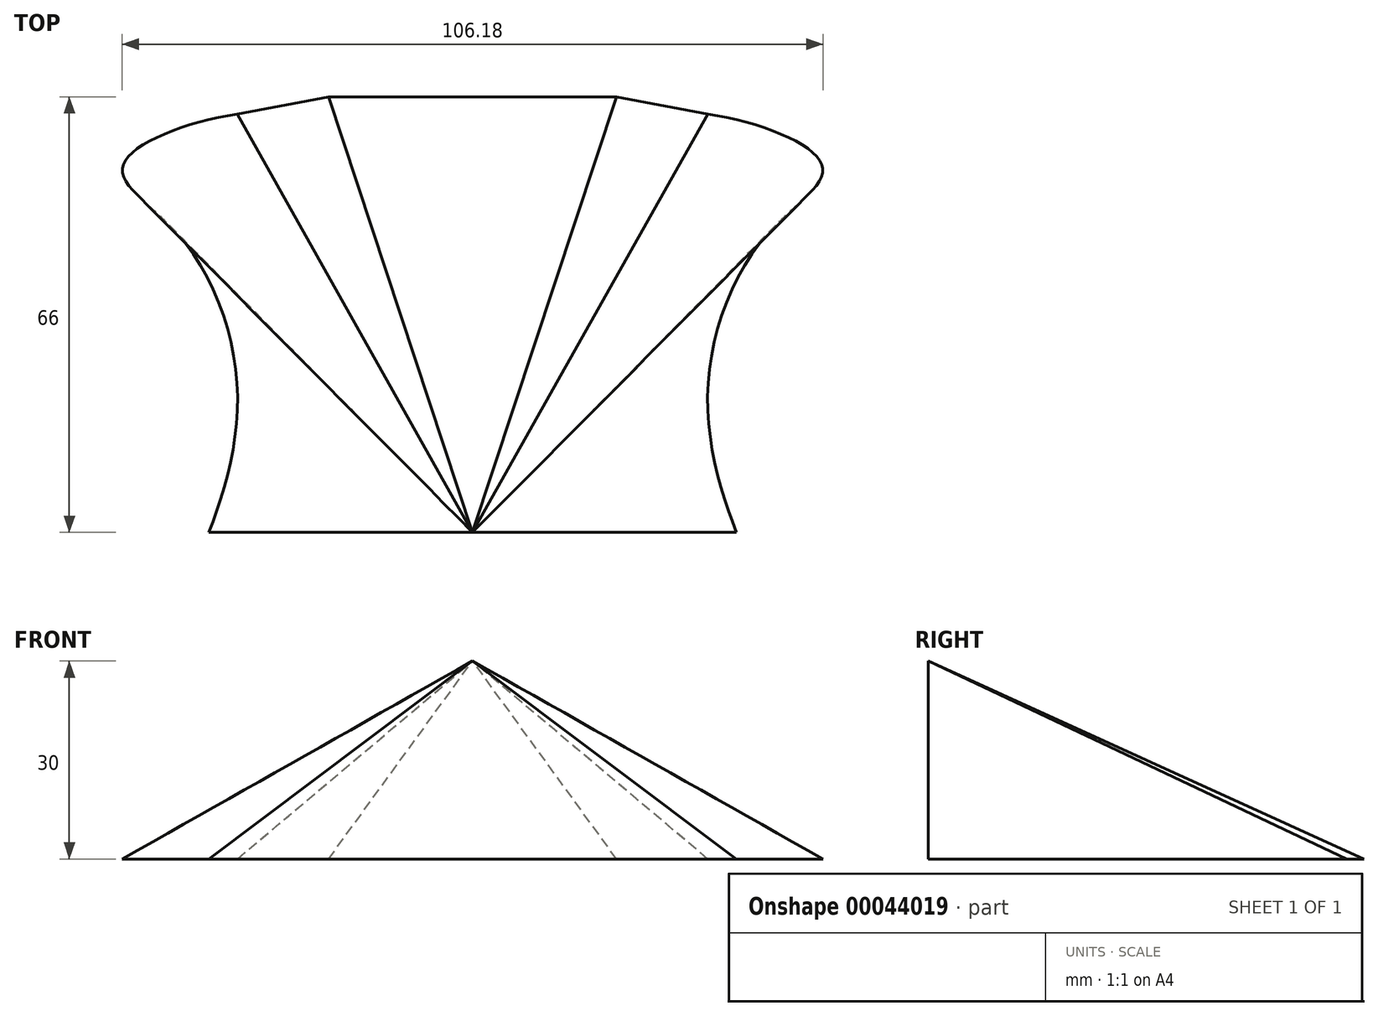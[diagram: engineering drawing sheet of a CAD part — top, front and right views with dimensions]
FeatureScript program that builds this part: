
annotation { "Feature Type Name" : "Feature", "Feature Type Description" : "" }
export const myFeature = defineFeature(function(context is Context, id is Id, definition is map)
    precondition{}
    {
        {
            var Q0;
            Q0=qCreatedBy(makeId("Top.planeOp"),FACE);
            var sketch = newSketch(context, id + "F0", { "sketchPlane" : qUnion([Q0])});
            skFitSpline(sketch, "E0", {"points": [v(-35.66, 21.54) * mm, v(-53.04, 13.52) * mm, v(-44.8, 3.49) * mm, v(-35.66, -19.99) * mm, v(-40, -41.85) * mm], "startDerivative": vector(-95.8, -14.73) * mm, "endDerivative": vector(-27.77, -69.38) * mm});
            skLineSegment(sketch, "E1", {"start": v(-40, -41.85) * mm, "end": v(0, -41.85) * mm});
            skLineSegment(sketch, "E2", {"start": v(-35.66, 21.54) * mm, "end": v(-21.83, 24.15) * mm});
            skLineSegment(sketch, "E3", {"start": v(-21.83, 24.15) * mm, "end": v(0, 24.15) * mm});
            skLineSegment(sketch, "E4.MirrorCS", {"start": v(35.66, 21.54) * mm, "end": v(21.83, 24.15) * mm});
            skLineSegment(sketch, "E5.MirrorCS", {"start": v(21.83, 24.15) * mm, "end": v(0, 24.15) * mm});
            skFitSpline(sketch, "E6.MirrorCS", {"points": [v(35.66, 21.54) * mm, v(53.04, 13.52) * mm, v(44.8, 3.49) * mm, v(35.66, -19.99) * mm, v(40, -41.85) * mm], "startDerivative": vector(95.8, -14.73) * mm, "endDerivative": vector(27.77, -69.38) * mm});
            skLineSegment(sketch, "E7.MirrorCS", {"start": v(40, -41.85) * mm, "end": v(0, -41.85) * mm});
            skSolve(sketch);
        }
        {
            var Q0;
            Q0=qCreatedBy(makeId("Top.planeOp"),FACE);
            cPlane(context, id + "F1", {"entities" : qUnion([Q0]), "cplaneType" : CPlaneType.OFFSET, "offset" : 30 * mm, "width" : 150 * mm, "height" : 150 * mm});
        }
        {
            var Q0;
            Q0=qCreatedBy(id+"F1.planeOp",FACE);
            var sketch = newSketch(context, id + "F2", { "sketchPlane" : qUnion([Q0])});
            skPoint(sketch, "E8", {"position": v(0, -41.85) * mm});
            skSolve(sketch);
        }
        {
            var Q0;
            Q0=makeQuery(id+"F0.imprint","IMPRINT",FACE,{"disambiguationData":[TD([[makeQuery(id+"F0.imprint","IMPRINT",EDGE,{"derivedFrom":sQuery(id+"F0.wireOp",EDGE,"E0")}),1.0]])]});
            var Q1;
            Q1=sQuery(id+"F2.wireOp",VERTEX,"E8");
            var Q2;
            Q2=makeQuery(id+"F0.imprint","IMPRINT",FACE,{"disambiguationData":[TD([[makeQuery(id+"F0.imprint","IMPRINT",EDGE,{"derivedFrom":sQuery(id+"F0.wireOp",EDGE,"E0")}),1.0]])]});
            var Q3;
            Q3=sQuery(id+"F2.wireOp",VERTEX,"E8");
            loft(context, id + "F3", {"sheetProfilesArray" : [{ "sheetProfileEntities" : qUnion([Q0]) }, { "sheetProfileEntities" : qUnion([Q1]) }], "wireProfilesArray" : [{ "wireProfileEntities" : qUnion([Q2]) }, { "wireProfileEntities" : qUnion([Q3]) }]});
        }
    });
